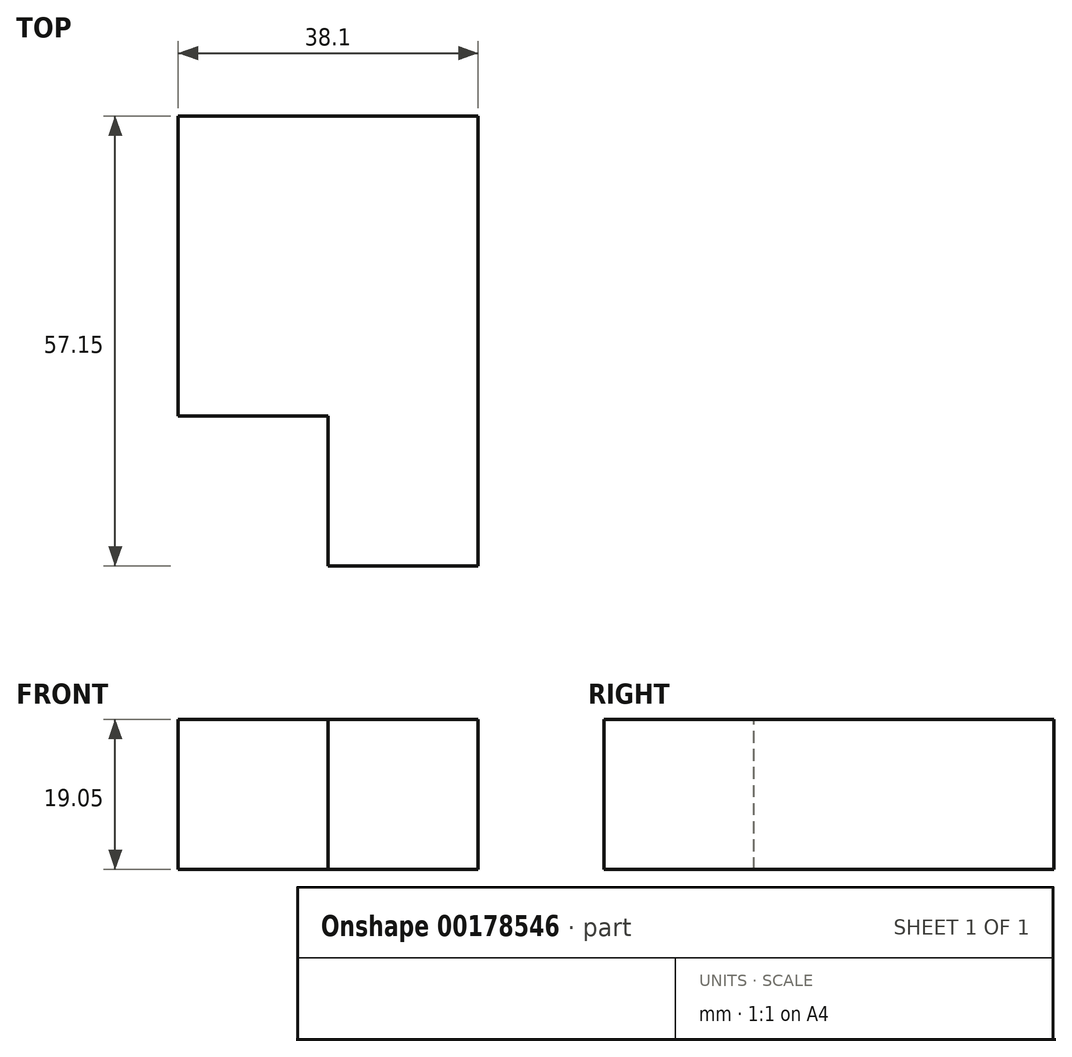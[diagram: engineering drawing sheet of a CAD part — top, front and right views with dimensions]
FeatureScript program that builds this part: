
annotation { "Feature Type Name" : "Feature", "Feature Type Description" : "" }
export const myFeature = defineFeature(function(context is Context, id is Id, definition is map)
    precondition{}
    {
        {
            var Q0;
            Q0=qCreatedBy(makeId("Front.planeOp"),FACE);
            var sketch = newSketch(context, id + "F0", { "sketchPlane" : qUnion([Q0])});
            skLineSegment(sketch, "E0.bottom", {"start": v(-82.91, 0) * mm, "end": v(-63.86, 0) * mm});
            skLineSegment(sketch, "E0.top", {"start": v(-82.91, 19.05) * mm, "end": v(-63.86, 19.05) * mm});
            skLineSegment(sketch, "E0.left", {"start": v(-82.91, 0) * mm, "end": v(-82.91, 19.05) * mm});
            skLineSegment(sketch, "E0.right", {"start": v(-63.86, 0) * mm, "end": v(-63.86, 19.05) * mm});
            skLineSegment(sketch, "E1.bottom", {"start": v(-63.86, 0) * mm, "end": v(-44.81, 0) * mm});
            skLineSegment(sketch, "E1.top", {"start": v(-63.86, 19.05) * mm, "end": v(-44.81, 19.05) * mm});
            skLineSegment(sketch, "E1.right", {"start": v(-44.81, 0) * mm, "end": v(-44.81, 19.05) * mm});
            skSolve(sketch);
        }
        {
            var Q0;
            Q0=makeQuery(id+"F0.imprint","IMPRINT",FACE,{"disambiguationData":[TD([[makeQuery(id+"F0.imprint","IMPRINT",EDGE,{"derivedFrom":sQuery(id+"F0.wireOp",EDGE,"E0.bottom")}),1.0]])]});
            extrude(context, id + "F1", {"entities" : qUnion([Q0]), "depth" : 38.1 * mm});
        }
        {
            var Q0;
            Q0=makeQuery(id+"F0.imprint","IMPRINT",FACE,{"disambiguationData":[TD([[makeQuery(id+"F0.imprint","IMPRINT",EDGE,{"derivedFrom":sQuery(id+"F0.wireOp",EDGE,"E1.bottom")}),1.0]])]});
            extrude(context, id + "F2", {"entities" : qUnion([Q0]), "operationType" : NewBodyOperationType.ADD, "depth" : 57.15 * mm});
        }
    });
